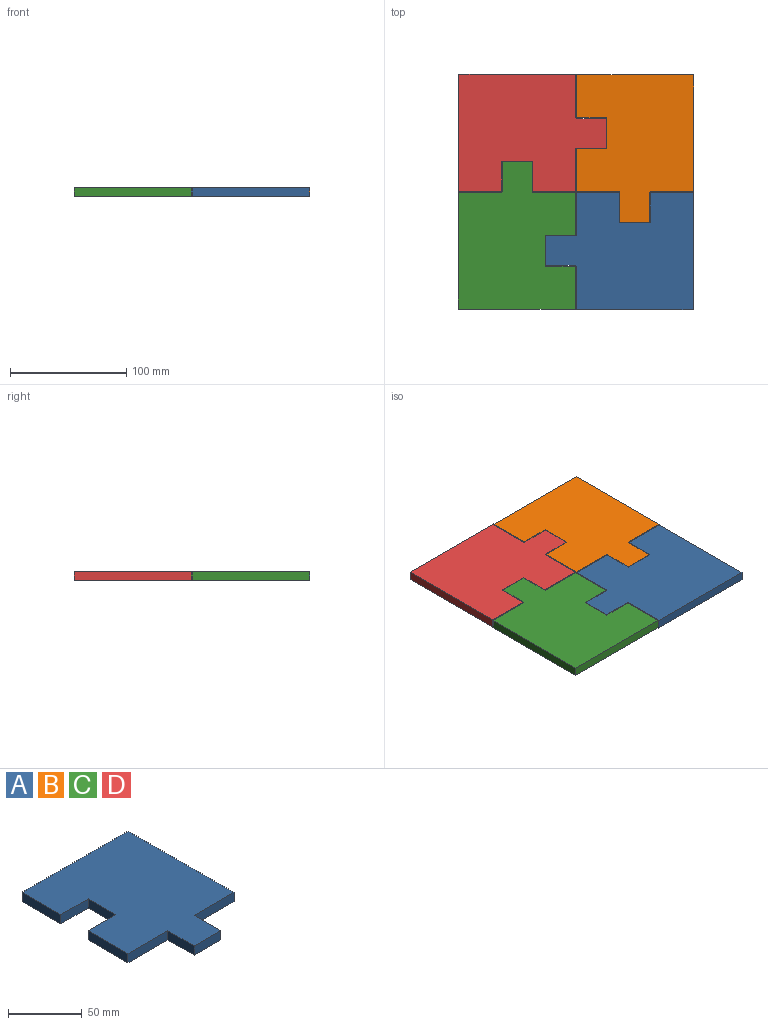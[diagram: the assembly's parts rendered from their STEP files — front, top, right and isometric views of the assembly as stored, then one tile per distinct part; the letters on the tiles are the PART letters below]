
ASSEMBLY  parts=4 mates=3
PART A: 14 faces, bbox 101.6x127x7.6 mm
  f0: plane 101.6x7.62mm, normal (1,0,0), area 774.2mm2, adj f1,f11,f12,f13
  f1: plane 101.6x7.62mm, normal (0,1,0), area 774.2mm2, adj f0,f2,f12,f13
  f2: plane 37.08x7.62mm, normal (-1,0,0), area 282.6mm2, adj f1,f3,f12,f13
  f3: plane 26.42x7.62mm, normal (0,-1,0), area 201.3mm2, adj f2,f4,f12,f13
  f4: plane 26.42x7.62mm, normal (-1,0,0), area 201.3mm2, adj f3,f5,f12,f13
  f5: plane 26.42x7.62mm, normal (0,1,0), area 201.3mm2, adj f4,f6,f12,f13
  f6: plane 38.1x7.62mm, normal (-1,0,0), area 290.3mm2, adj f5,f7,f12,f13
  f7: plane 38.1x7.62mm, normal (0,-1,0), area 290.3mm2, adj f6,f8,f12,f13
  f8: plane 25.4x7.62mm, normal (-1,0,0), area 193.5mm2, adj f7,f9,f12,f13
  f9: plane 25.4x7.62mm, normal (0,-1,0), area 193.5mm2, adj f8,f10,f12,f13
  f10: plane 25.4x7.62mm, normal (1,0,0), area 193.5mm2, adj f9,f11,f12,f13
  f11: plane 38.1x7.62mm, normal (0,-1,0), area 290.3mm2, adj f0,f10,f12,f13
  f12: plane 127x101.6mm, normal (0,0,1), area 10269.9mm2, adj f0,f1,f2,f3,f4,f5,f6,f7
  f13: plane 127x101.6mm, normal (0,0,-1), area 10269.9mm2, adj f0,f1,f2,f3,f4,f5,f6,f7
PART B: same geometry as A
PART C: same geometry as A
PART D: same geometry as A
PLACE A rot(axis=(0,0,-1),90deg) t=(-32.29,-147.81,20.93)mm
PLACE B t=(-31.78,-47.22,20.93)mm
PLACE C rot(axis=(0,0,1),180deg) t=(-132.87,-147.3,20.93)mm
PLACE D rot(axis=(0,0,1),90deg) t=(-132.36,-46.71,20.93)mm
MATE fastened D.f12 <-> C.f12  axis (0,0,1) through (-132.87,-71.1,28.55)mm
MATE fastened B.f12 <-> A.f12  axis (0,0,1) through (-31.78,-123.42,28.55)mm
MATE fastened A.f12 <-> C.f12  axis (0,0,1) through (-108.49,-147.81,28.55)mm
